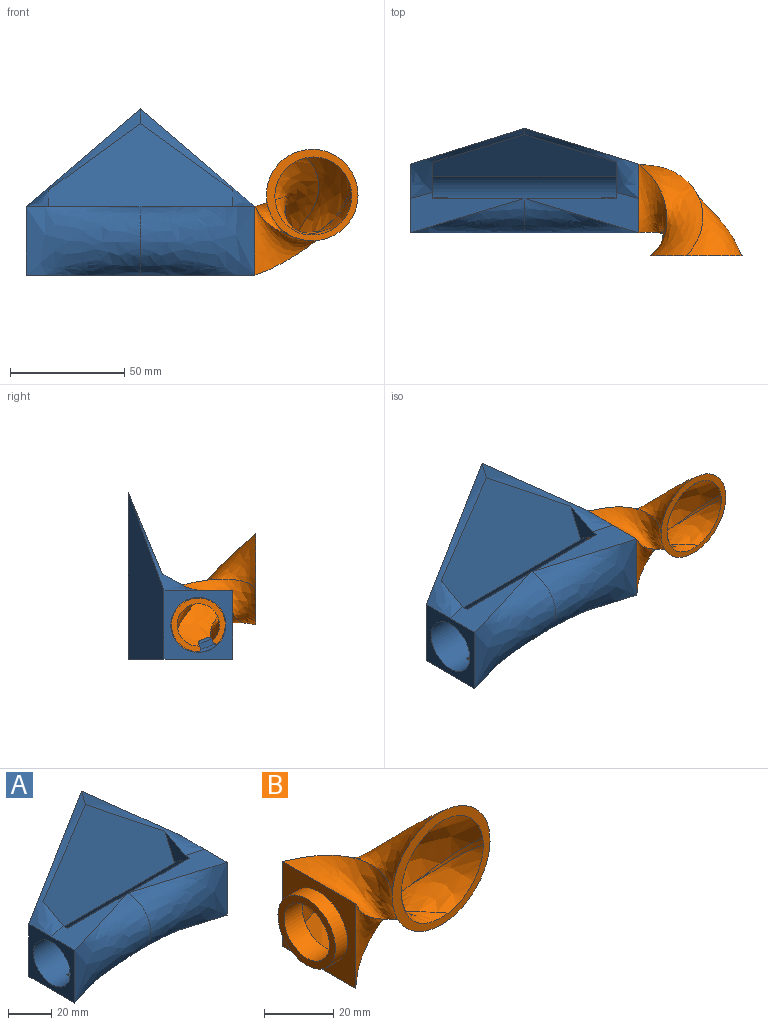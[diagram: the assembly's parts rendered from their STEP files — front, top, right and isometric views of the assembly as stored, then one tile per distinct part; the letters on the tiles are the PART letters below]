
ASSEMBLY  parts=2 mates=1
PART A: 42 faces, bbox 100x45.5x72.7 mm
  f0: cylinder r=12mm len=100mm, axis (1,0,0), area 6407mm2, adj f4,f9,f12,f13,f14,f15,f34,f35
  f1: bspline ~50x42.69mm, area 363.1mm2, adj f2,f3,f4,f8,f12,f14
  f2: plane 49.17x17.55mm, normal (0,0,1), area 377.9mm2, adj f1,f4,f6,f13,f14
  f3: bspline ~50x42.69mm, area 363.1mm2, adj f1,f5,f9,f11,f12,f15
  f4: plane 30x30mm, normal (-1,0,0), area 447.6mm2, adj f0,f1,f2,f6,f7,f8
  f5: plane 49.17x17.55mm, normal (0,0,1), area 377.9mm2, adj f3,f9,f10,f13,f15
  f6: bspline ~50x30mm, area 1813.5mm2, adj f2,f4,f7,f10,f13
  f7: plane 100x45.54mm, normal (0,0,-1), area 3026.9mm2, adj f4,f6,f8,f9,f10,f11
  f8: plane 72.69x50mm, normal (-0.3,0.95,0), area 2688.4mm2, adj f1,f4,f7,f11
  f9: plane 30x30mm, normal (1,0,0), area 447.6mm2, adj f0,f3,f5,f7,f10,f11
  f10: bspline ~50x30mm, area 1813.5mm2, adj f5,f6,f7,f9,f13
  f11: plane 72.69x50mm, normal (0.3,0.95,0), area 2688.4mm2, adj f3,f7,f8,f9
  f12: plane 80x44mm, normal (0,-0.92,0.38), area 2555.6mm2, adj f0,f1,f3,f14,f15
  f13: plane 80x3.1mm, normal (0,0.92,-0.38), area 268.6mm2, adj f0,f2,f5,f6,f10,f14,f15
  f14: plane 17.32x14.97mm, normal (1,0,0), area 94.3mm2, adj f0,f1,f2,f12,f13
  f15: plane 17.32x14.97mm, normal (-1,0,0), area 94.3mm2, adj f0,f3,f5,f12,f13
  f16: plane 3x1.49mm, normal (0,-0.92,0.38), area 4.9mm2, adj f19,f20,f30,f41
  f17: plane 3x1.49mm, normal (0,0.92,-0.38), area 4.9mm2, adj f19,f20,f33,f38
  f18: plane 3.23x1.35mm, normal (0,0.38,0.92), area 1.8mm2, adj f30,f31,f32,f33
  f19: plane 6.46x4.34mm, normal (1,0,0), area 15mm2, adj f16,f17,f31,f38,f39,f41
  f20: plane 6.46x4.34mm, normal (-1,0,0), area 15mm2, adj f16,f17,f32,f38,f40,f41
  f21: plane 3x1.49mm, normal (0,-0.92,0.38), area 4.9mm2, adj f24,f25,f26,f37
  f22: plane 3x1.49mm, normal (0,0.92,-0.38), area 4.9mm2, adj f24,f25,f29,f34
  f23: plane 3.23x1.35mm, normal (0,0.38,0.92), area 1.8mm2, adj f26,f27,f28,f29
  f24: plane 6.46x4.34mm, normal (-1,0,0), area 15mm2, adj f21,f22,f27,f34,f35,f37
  f25: plane 6.46x4.34mm, normal (1,0,0), area 15mm2, adj f21,f22,f28,f34,f36,f37
  f26: cylinder r=1.25mm len=3mm, axis (-1,0,0), area 4.1mm2, adj f21,f23,f27,f28
  f27: cylinder r=1.25mm len=6.02mm, axis (0,0.92,-0.38), area 9.3mm2, adj f23,f24,f26,f29
  f28: cylinder r=1.25mm len=6.02mm, axis (0,-0.92,0.38), area 9.3mm2, adj f23,f25,f26,f29
  f29: cylinder r=1.25mm len=3mm, axis (1,0,0), area 4.1mm2, adj f22,f23,f27,f28
  f30: cylinder r=1.25mm len=3mm, axis (-1,0,0), area 4.1mm2, adj f16,f18,f31,f32
  f31: cylinder r=1.25mm len=6.02mm, axis (0,0.92,-0.38), area 9.3mm2, adj f18,f19,f30,f33
  f32: cylinder r=1.25mm len=6.02mm, axis (0,-0.92,0.38), area 9.3mm2, adj f18,f20,f30,f33
  f33: cylinder r=1.25mm len=3mm, axis (1,0,0), area 4.1mm2, adj f17,f18,f31,f32
  f34: cylinder r=1.5mm len=6mm, axis (1,0,0), area 12.8mm2, adj f0,f22,f24,f25,f35,f36
  f35: torus R=10.5mm, axis (1,0,0), area 20.1mm2, adj f0,f24,f34,f37
  f36: torus R=10.5mm, axis (1,0,0), area 20.1mm2, adj f0,f25,f34,f37
  f37: cylinder r=1.5mm len=6mm, axis (1,0,0), area 12.8mm2, adj f0,f21,f24,f25,f35,f36
  f38: cylinder r=1.5mm len=6mm, axis (1,0,0), area 12.8mm2, adj f0,f17,f19,f20,f39,f40
  f39: torus R=10.5mm, axis (1,0,0), area 20.1mm2, adj f0,f19,f38,f41
  f40: torus R=10.5mm, axis (1,0,0), area 20.1mm2, adj f0,f20,f38,f41
  f41: cylinder r=1.5mm len=6mm, axis (1,0,0), area 12.8mm2, adj f0,f16,f19,f20,f39,f40
PART B: 17 faces, bbox 55x45.7x61.3 mm
  f0: cylinder r=11.75mm len=23.5mm, axis (1,0,0), area 369.1mm2, adj f1,f2
  f1: plane 23.5x23.5mm, normal (-1,0,0), area 164.9mm2, adj f0,f11
  f2: plane 30x30mm, normal (-1,0,0), area 466.3mm2, adj f0,f4,f5,f6,f7
  f3: plane 40.99x40.99mm, normal (0,-1,0), area 359.3mm2, adj f4,f5,f6,f7,f8,f13,f14,f15
  f4: bspline ~40.41x29.36mm, area 651.4mm2, adj f2,f3,f5,f7
  f5: bspline ~45x38.92mm, area 882mm2, adj f2,f3,f4,f6
  f6: bspline ~55.54x45.4mm, area 1475.4mm2, adj f2,f3,f5,f7
  f7: bspline ~55.92x40.72mm, area 1266.5mm2, adj f2,f3,f4,f6
  f8: offset ~48.17x36.14mm, area 613.9mm2, adj f3,f9,f10,f12,f13,f14,f15
  f9: offset ~20.58x13.84mm, area 0.1mm2, adj f8,f12,f15
  f10: bspline ~5.33x4.49mm, area 1mm2, adj f8,f14,f15
  f11: cylinder r=9.25mm len=18.5mm, axis (1,0,0), area 435.9mm2, adj f1,f12
  f12: plane 27.71x27.41mm, normal (1,0,0), area 213.2mm2, adj f8,f9,f11,f13,f15,f16
  f13: offset ~45.14x34.48mm, area 492.9mm2, adj f3,f8,f12,f16
  f14: offset ~23.08x19.67mm, area 26.1mm2, adj f3,f8,f10,f15
  f15: offset ~60.18x49.91mm, area 1013.4mm2, adj f3,f8,f9,f10,f12,f14,f16
  f16: offset ~60.29x45.24mm, area 921mm2, adj f3,f12,f13,f15
PLACE A t=(5.89,4.21,-4.16)mm
PLACE B t=(55.89,4.21,-4.16)mm
MATE fastened B.f0 <-> A.f0  axis (-1,0,0) through (55.89,4.21,-4.16)mm
